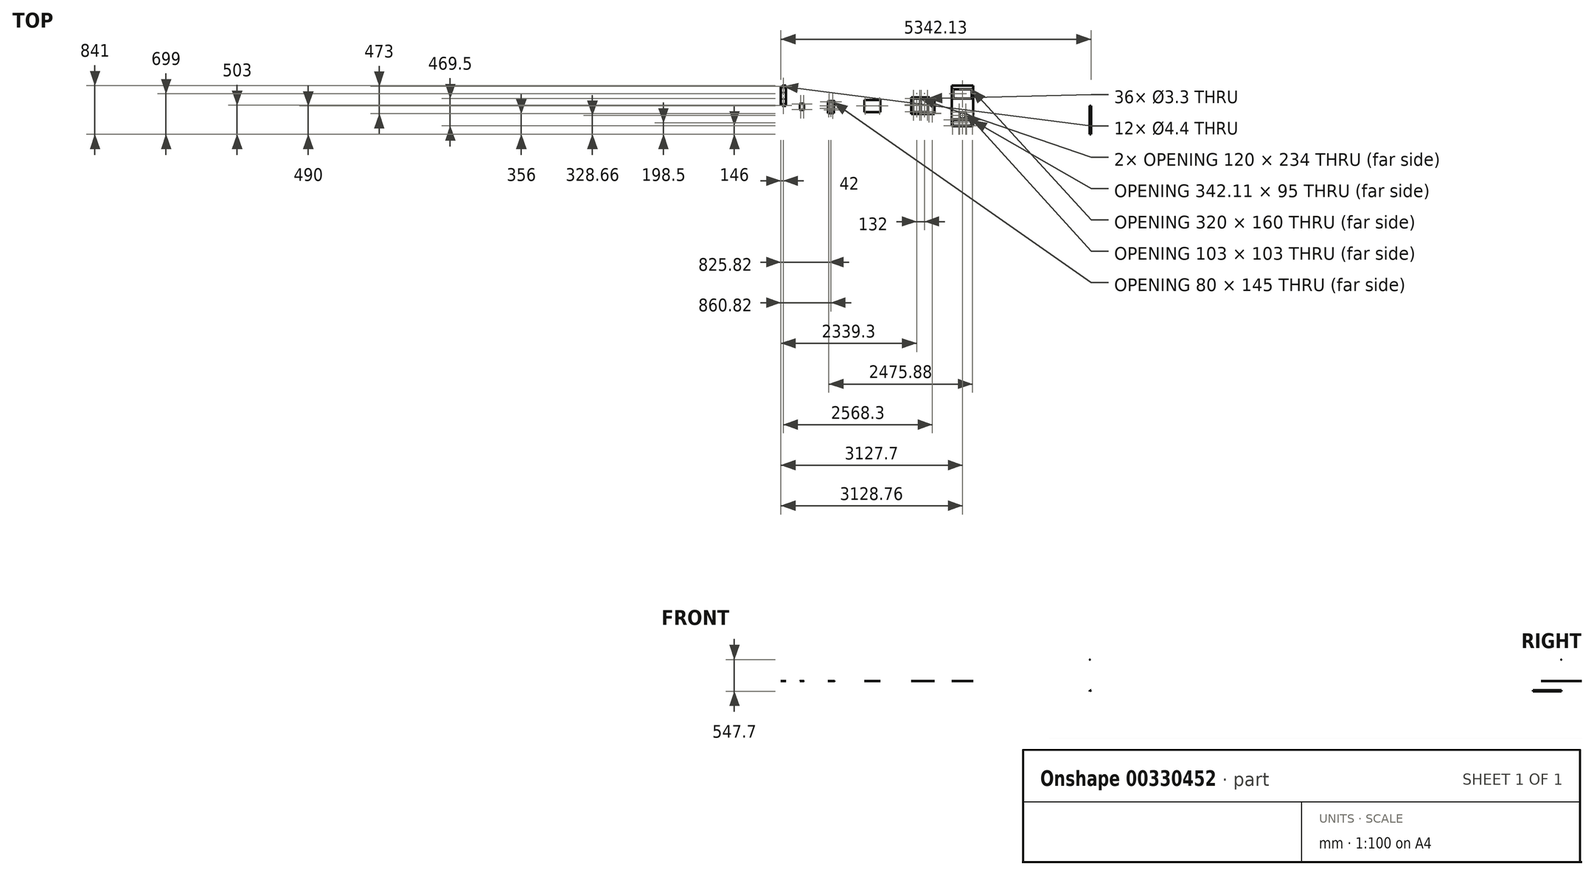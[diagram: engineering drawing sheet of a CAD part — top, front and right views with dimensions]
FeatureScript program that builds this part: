
annotation { "Feature Type Name" : "Feature", "Feature Type Description" : "" }
export const myFeature = defineFeature(function(context is Context, id is Id, definition is map)
    precondition{}
    {
        {
            var Q0;
            Q0=qCreatedBy(makeId("Top.planeOp"),FACE);
            var sketch = newSketch(context, id + "F0", { "sketchPlane" : qUnion([Q0])});
            skLineSegment(sketch, "E0.bottom", {"start": v(-184, -349) * mm, "end": v(-170, -349) * mm});
            skLineSegment(sketch, "E0.top", {"start": v(-184, 349) * mm, "end": v(184, 349) * mm});
            skLineSegment(sketch, "E0.left", {"start": v(-184, -349) * mm, "end": v(-184, 349) * mm});
            skLineSegment(sketch, "E0.right", {"start": v(184, -349) * mm, "end": v(184, 349) * mm});
            skPoint(sketch, "E0.middle", {"position": v(0, 0) * mm});
            skPoint(sketch, "E1.endSnap0", {"position": v(0, 349) * mm});
            skPoint(sketch, "E2.endSnap0", {"position": v(-184, 0) * mm});
            skPoint(sketch, "E3.positionSnap0", {"position": v(184, 0) * mm});
            skPoint(sketch, "E4", {"position": v(-170, -349) * mm});
            skPoint(sketch, "E5", {"position": v(-170, -244) * mm});
            skLineSegment(sketch, "E6", {"start": v(-165, -244) * mm, "end": v(0, -244) * mm});
            skLineSegment(sketch, "E7.MirrorCS", {"start": v(165.12, -244) * mm, "end": v(0, -244) * mm});
            skPoint(sketch, "E1.start.orphan", {"position": v(0, 349) * mm});
            skLineSegment(sketch, "E8.trimOffspring", {"start": v(170, -349) * mm, "end": v(184, -349) * mm});
            skLineSegment(sketch, "E9", {"start": v(170, -349) * mm, "end": v(-170, -349) * mm});
            skLineSegment(sketch, "E10", {"start": v(167.11, -339) * mm, "end": v(-164.96, -339) * mm});
            skLineSegment(sketch, "E11", {"start": v(170.11, -248.88) * mm, "end": v(172.11, -333.88) * mm});
            skLineSegment(sketch, "E12", {"start": v(-170, -249) * mm, "end": v(-169.96, -334) * mm});
            skPoint(sketch, "E13.visualSharp", {"position": v(172.23, -339) * mm});
            skArc(sketch, "E13.filletArc", {"start": v(167.11, -339) * mm, "mid": v(170.69, -337.5) * mm, "end": v(172.11, -333.88) * mm});
            skPoint(sketch, "E14.visualSharp", {"position": v(170, -244) * mm});
            skArc(sketch, "E14.filletArc", {"start": v(170.11, -248.88) * mm, "mid": v(168.6, -245.42) * mm, "end": v(165.12, -244) * mm});
            skArc(sketch, "E15.filletArc", {"start": v(-165, -244) * mm, "mid": v(-168.53, -245.47) * mm, "end": v(-170, -249) * mm});
            skPoint(sketch, "E16.visualSharp", {"position": v(-169.96, -339) * mm});
            skArc(sketch, "E16.filletArc", {"start": v(-169.96, -334) * mm, "mid": v(-168.5, -337.54) * mm, "end": v(-164.96, -339) * mm});
            skLineSegment(sketch, "E17.bottom", {"start": v(155, 289) * mm, "end": v(-155, 289) * mm});
            skLineSegment(sketch, "E17.top", {"start": v(155, 129) * mm, "end": v(-155, 129) * mm});
            skLineSegment(sketch, "E17.left", {"start": v(160, 284) * mm, "end": v(160, 134) * mm});
            skLineSegment(sketch, "E17.right", {"start": v(-160, 284) * mm, "end": v(-160, 134) * mm});
            skPoint(sketch, "E17.middle", {"position": v(0, 209) * mm});
            skPoint(sketch, "E18.visualSharp", {"position": v(160, 129) * mm});
            skArc(sketch, "E18.filletArc", {"start": v(155, 129) * mm, "mid": v(158.54, 130.46) * mm, "end": v(160, 134) * mm});
            skPoint(sketch, "E19.visualSharp", {"position": v(-160, 129) * mm});
            skArc(sketch, "E19.filletArc", {"start": v(-160, 134) * mm, "mid": v(-158.54, 130.46) * mm, "end": v(-155, 129) * mm});
            skPoint(sketch, "E20.visualSharp", {"position": v(-160, 289) * mm});
            skArc(sketch, "E20.filletArc", {"start": v(-155, 289) * mm, "mid": v(-158.54, 287.54) * mm, "end": v(-160, 284) * mm});
            skPoint(sketch, "E21.visualSharp", {"position": v(160, 289) * mm});
            skArc(sketch, "E21.filletArc", {"start": v(160, 284) * mm, "mid": v(158.54, 287.54) * mm, "end": v(155, 289) * mm});
            skLineSegment(sketch, "E22", {"start": v(171.11, -291.38) * mm, "end": v(-169.98, -291.5) * mm, "construction": true});
            skPoint(sketch, "E23", {"position": v(-169, -344) * mm});
            skPoint(sketch, "E24", {"position": v(-64, -344) * mm});
            skPoint(sketch, "E25", {"position": v(-50, -344) * mm});
            skPoint(sketch, "E26", {"position": v(55, -344) * mm});
            skPoint(sketch, "E27", {"position": v(69, -344) * mm});
            skPoint(sketch, "E28", {"position": v(174, -344) * mm});
            skCircle(sketch, "E29", {"center": v(-169, -344) * mm, "radius": 1.65 * mm});
            skCircle(sketch, "E30", {"center": v(-64, -344) * mm, "radius": 1.65 * mm});
            skCircle(sketch, "E31", {"center": v(-50, -344) * mm, "radius": 1.65 * mm});
            skCircle(sketch, "E32", {"center": v(55, -344) * mm, "radius": 1.65 * mm});
            skCircle(sketch, "E33", {"center": v(69, -344) * mm, "radius": 1.65 * mm});
            skCircle(sketch, "E34", {"center": v(174, -344) * mm, "radius": 1.65 * mm});
            skPoint(sketch, "E35.MirrorP", {"position": v(54.96, -238.84) * mm});
            skPoint(sketch, "E36.MirrorP", {"position": v(68.96, -238.83) * mm});
            skPoint(sketch, "E37.MirrorP", {"position": v(173.96, -238.76) * mm});
            skCircle(sketch, "E38.MirrorC", {"center": v(-50.04, -238.92) * mm, "radius": 1.65 * mm});
            skCircle(sketch, "E39.MirrorC", {"center": v(-64.04, -238.93) * mm, "radius": 1.65 * mm});
            skPoint(sketch, "E40.MirrorP", {"position": v(-169.04, -239) * mm});
            skCircle(sketch, "E41.MirrorC", {"center": v(-169.04, -239) * mm, "radius": 1.65 * mm});
            skCircle(sketch, "E42.MirrorC", {"center": v(54.96, -238.84) * mm, "radius": 1.65 * mm});
            skCircle(sketch, "E43.MirrorC", {"center": v(68.96, -238.83) * mm, "radius": 1.65 * mm});
            skCircle(sketch, "E44.MirrorC", {"center": v(173.96, -238.76) * mm, "radius": 1.65 * mm});
            skCircle(sketch, "E45", {"center": v(54.96, -213.84) * mm, "radius": 1.65 * mm});
            skLineSegment(sketch, "E46", {"start": v(0, -244) * mm, "end": v(0, -229.93) * mm, "construction": true});
            skCircle(sketch, "E47", {"center": v(54.96, -108.84) * mm, "radius": 1.65 * mm});
            skCircle(sketch, "E48.MirrorC", {"center": v(-54.96, -213.84) * mm, "radius": 1.65 * mm});
            skCircle(sketch, "E49.MirrorC", {"center": v(-54.96, -108.84) * mm, "radius": 1.65 * mm});
            skLineSegment(sketch, "E50", {"start": v(-54.96, -108.84) * mm, "end": v(54.96, -213.84) * mm, "construction": true});
            skLineSegment(sketch, "E51.bottom", {"start": v(-46.5, -212.84) * mm, "end": v(46.5, -212.84) * mm});
            skLineSegment(sketch, "E51.top", {"start": v(-46.5, -109.84) * mm, "end": v(46.5, -109.84) * mm});
            skLineSegment(sketch, "E51.left", {"start": v(-51.5, -207.84) * mm, "end": v(-51.5, -114.84) * mm});
            skLineSegment(sketch, "E51.right", {"start": v(51.5, -207.84) * mm, "end": v(51.5, -114.84) * mm});
            skPoint(sketch, "E51.middle", {"position": v(0, -161.34) * mm});
            skPoint(sketch, "E52.visualSharp", {"position": v(51.5, -212.84) * mm});
            skArc(sketch, "E52.filletArc", {"start": v(46.5, -212.84) * mm, "mid": v(50.04, -211.38) * mm, "end": v(51.5, -207.84) * mm});
            skPoint(sketch, "E53.visualSharp", {"position": v(51.5, -109.84) * mm});
            skArc(sketch, "E53.filletArc", {"start": v(51.5, -114.84) * mm, "mid": v(50.04, -111.3) * mm, "end": v(46.5, -109.84) * mm});
            skPoint(sketch, "E54.visualSharp", {"position": v(-51.5, -109.84) * mm});
            skArc(sketch, "E54.filletArc", {"start": v(-46.5, -109.84) * mm, "mid": v(-50.04, -111.3) * mm, "end": v(-51.5, -114.84) * mm});
            skPoint(sketch, "E55.visualSharp", {"position": v(-51.5, -212.84) * mm});
            skArc(sketch, "E55.filletArc", {"start": v(-51.5, -207.84) * mm, "mid": v(-50.04, -211.38) * mm, "end": v(-46.5, -212.84) * mm});
            skSolve(sketch);
        }
        {
            var Q0;
            {var subQ1=sQuery(id+"F0.wireOp",EDGE,"E0.bottom");Q0=makeQuery(id+"F0.imprint","IMPRINT",FACE,{"disambiguationData":[TD([[makeQuery(id+"F0.imprint","IMPRINT",EDGE,{"derivedFrom":subQ1}),1.0]])]});}
            extrude(context, id + "F1", {"entities" : qUnion([Q0]), "depth" : 3 * mm});
        }
        {
            var Q0;
            Q0=qCreatedBy(makeId("Top.planeOp"),FACE);
            var sketch = newSketch(context, id + "F2", { "sketchPlane" : qUnion([Q0])});
            skLineSegment(sketch, "E56.bottom", {"start": v(-881.4, -140) * mm, "end": v(-701.4, -140) * mm});
            skLineSegment(sketch, "E56.left", {"start": v(-881.4, -140) * mm, "end": v(-881.4, 150) * mm});
            skPoint(sketch, "E56.middle", {"position": v(-788.4, 15.4) * mm});
            skPoint(sketch, "E57", {"position": v(-869.4, 150) * mm});
            skLineSegment(sketch, "E58", {"start": v(-788.4, 15.4) * mm, "end": v(-788.4, 43.03) * mm, "construction": true});
            skLineSegment(sketch, "E59", {"start": v(-788.4, 15.4) * mm, "end": v(-811.31, 15.4) * mm, "construction": true});
            skPoint(sketch, "E60", {"position": v(-869.4, 10) * mm});
            skPoint(sketch, "E61", {"position": v(-869.4, 132) * mm});
            skPoint(sketch, "E62", {"position": v(-725.4, -104) * mm});
            skPoint(sketch, "E63.MirrorP", {"position": v(-848.4, -104) * mm});
            skPoint(sketch, "E64.MirrorP", {"position": v(-725.4, 130) * mm});
            skPoint(sketch, "E65.MirrorP", {"position": v(-848.4, 130) * mm});
            skLineSegment(sketch, "E66", {"start": v(-837.4, 130) * mm, "end": v(-739.4, 130) * mm});
            skLineSegment(sketch, "E67", {"start": v(-728.4, -95) * mm, "end": v(-728.4, 1) * mm});
            skLineSegment(sketch, "E68", {"start": v(-739.4, -104) * mm, "end": v(-839.4, -104) * mm});
            skLineSegment(sketch, "E69", {"start": v(-848.4, -95) * mm, "end": v(-848.4, 1) * mm});
            skPoint(sketch, "E70", {"position": v(-848.4, -95) * mm});
            skPoint(sketch, "E71", {"position": v(-839.4, -104) * mm});
            skLineSegment(sketch, "E72", {"start": v(-837.4, -104) * mm, "end": v(-837.4, -95) * mm});
            skLineSegment(sketch, "E73", {"start": v(-837.4, -95) * mm, "end": v(-846.4, -95) * mm});
            skCircle(sketch, "E74", {"center": v(-840.9, -99.5) * mm, "radius": 1.65 * mm});
            skLineSegment(sketch, "E75.MirrorCS", {"start": v(-739.4, -104) * mm, "end": v(-739.4, -95) * mm});
            skPoint(sketch, "E76.MirrorP", {"position": v(-725.4, -95) * mm});
            skLineSegment(sketch, "E77.MirrorCS", {"start": v(-739.4, -95) * mm, "end": v(-730.4, -95) * mm});
            skCircle(sketch, "E78.MirrorC", {"center": v(-735.9, -99.5) * mm, "radius": 1.65 * mm});
            skLineSegment(sketch, "E79.MirrorCS", {"start": v(-837.4, 130) * mm, "end": v(-837.4, 121) * mm});
            skLineSegment(sketch, "E80.MirrorCS", {"start": v(-839.4, 121) * mm, "end": v(-848.4, 121) * mm});
            skCircle(sketch, "E81.MirrorC", {"center": v(-840.9, 125.5) * mm, "radius": 1.65 * mm});
            skLineSegment(sketch, "E82.MirrorCS", {"start": v(-737.4, 121) * mm, "end": v(-728.4, 121) * mm});
            skLineSegment(sketch, "E83.MirrorCS", {"start": v(-739.4, 130) * mm, "end": v(-739.4, 121) * mm});
            skCircle(sketch, "E84.MirrorC", {"center": v(-735.9, 125.5) * mm, "radius": 1.65 * mm});
            skLineSegment(sketch, "E85.MirrorCS", {"start": v(-837.4, 1) * mm, "end": v(-846.4, 1) * mm});
            skLineSegment(sketch, "E86.MirrorCS", {"start": v(-837.4, 10) * mm, "end": v(-837.4, 1) * mm});
            skCircle(sketch, "E87.MirrorC", {"center": v(-840.9, 5.5) * mm, "radius": 1.65 * mm});
            skCircle(sketch, "E88", {"center": v(-840.9, 20.5) * mm, "radius": 1.65 * mm});
            skPoint(sketch, "E89", {"position": v(-848.4, 25) * mm});
            skLineSegment(sketch, "E90", {"start": v(-846.4, 25) * mm, "end": v(-837.4, 25) * mm});
            skLineSegment(sketch, "E91", {"start": v(-837.4, 25) * mm, "end": v(-837.4, 10) * mm});
            skLineSegment(sketch, "E92.MirrorCS", {"start": v(-739.4, 1) * mm, "end": v(-730.4, 1) * mm});
            skLineSegment(sketch, "E93.MirrorCS", {"start": v(-739.4, 10) * mm, "end": v(-739.4, 1) * mm});
            skLineSegment(sketch, "E94.MirrorCS", {"start": v(-739.4, 25) * mm, "end": v(-739.4, 10) * mm});
            skLineSegment(sketch, "E95.MirrorCS", {"start": v(-730.4, 25) * mm, "end": v(-739.4, 25) * mm});
            skCircle(sketch, "E96.MirrorC", {"center": v(-735.9, 20.5) * mm, "radius": 1.65 * mm});
            skCircle(sketch, "E97.MirrorC", {"center": v(-735.9, 5.5) * mm, "radius": 1.65 * mm});
            skLineSegment(sketch, "E98", {"start": v(-848.4, 25) * mm, "end": v(-848.4, 121) * mm});
            skLineSegment(sketch, "E99", {"start": v(-728.4, 25) * mm, "end": v(-728.4, 121) * mm});
            skLineSegment(sketch, "E100", {"start": v(-737.4, 121) * mm, "end": v(-739.4, 121) * mm});
            skLineSegment(sketch, "E101", {"start": v(-837.4, 121) * mm, "end": v(-839.4, 121) * mm});
            skLineSegment(sketch, "E102", {"start": v(-728.4, 25) * mm, "end": v(-730.4, 25) * mm});
            skLineSegment(sketch, "E103", {"start": v(-730.4, 1) * mm, "end": v(-728.4, 1) * mm});
            skLineSegment(sketch, "E104", {"start": v(-846.4, 1) * mm, "end": v(-848.4, 1) * mm});
            skLineSegment(sketch, "E105", {"start": v(-846.4, 25) * mm, "end": v(-848.4, 25) * mm});
            skLineSegment(sketch, "E106", {"start": v(-730.4, -95) * mm, "end": v(-728.4, -95) * mm});
            skLineSegment(sketch, "E107", {"start": v(-846.4, -95) * mm, "end": v(-848.4, -95) * mm});
            skLineSegment(sketch, "E108.bottom", {"start": v(-759.4, -140) * mm, "end": v(-579.4, -140) * mm});
            skPoint(sketch, "E108.middle", {"position": v(-656.4, 6) * mm});
            skPoint(sketch, "E109", {"position": v(-743.4, 134) * mm});
            skLineSegment(sketch, "E110", {"start": v(-656.4, 6) * mm, "end": v(-656.4, 33.63) * mm, "construction": true});
            skLineSegment(sketch, "E111", {"start": v(-656.4, 6) * mm, "end": v(-679.31, 6) * mm, "construction": true});
            skPoint(sketch, "E112.MirrorP", {"position": v(-493.4, 30) * mm});
            skPoint(sketch, "E113.MirrorP", {"position": v(-493.4, -112) * mm});
            skPoint(sketch, "E114", {"position": v(-596.4, -104) * mm});
            skPoint(sketch, "E115.MirrorP", {"position": v(-717.4, -104) * mm});
            skPoint(sketch, "E116.MirrorP", {"position": v(-596.4, 130) * mm});
            skPoint(sketch, "E117.MirrorP", {"position": v(-717.4, 130) * mm});
            skLineSegment(sketch, "E118", {"start": v(-705.4, 130) * mm, "end": v(-607.4, 130) * mm});
            skLineSegment(sketch, "E119", {"start": v(-596.4, -95) * mm, "end": v(-596.4, 1) * mm});
            skLineSegment(sketch, "E120", {"start": v(-607.4, -104) * mm, "end": v(-705.4, -104) * mm});
            skLineSegment(sketch, "E121", {"start": v(-716.4, -95) * mm, "end": v(-716.4, 1) * mm});
            skPoint(sketch, "E122", {"position": v(-717.4, -95) * mm});
            skPoint(sketch, "E123", {"position": v(-707.4, -104) * mm});
            skLineSegment(sketch, "E124", {"start": v(-705.4, -104) * mm, "end": v(-705.4, -95) * mm});
            skLineSegment(sketch, "E125", {"start": v(-705.4, -95) * mm, "end": v(-714.4, -95) * mm});
            skCircle(sketch, "E126", {"center": v(-708.9, -99.5) * mm, "radius": 1.65 * mm});
            skLineSegment(sketch, "E127.MirrorCS", {"start": v(-607.4, -104) * mm, "end": v(-607.4, -95) * mm});
            skPoint(sketch, "E128.MirrorP", {"position": v(-596.4, -95) * mm});
            skLineSegment(sketch, "E129.MirrorCS", {"start": v(-607.4, -95) * mm, "end": v(-598.4, -95) * mm});
            skCircle(sketch, "E130.MirrorC", {"center": v(-603.9, -99.5) * mm, "radius": 1.65 * mm});
            skLineSegment(sketch, "E131.MirrorCS", {"start": v(-705.4, 130) * mm, "end": v(-705.4, 121) * mm});
            skLineSegment(sketch, "E132.MirrorCS", {"start": v(-707.4, 121) * mm, "end": v(-716.4, 121) * mm});
            skCircle(sketch, "E133.MirrorC", {"center": v(-708.9, 125.5) * mm, "radius": 1.65 * mm});
            skLineSegment(sketch, "E134.MirrorCS", {"start": v(-605.4, 121) * mm, "end": v(-596.4, 121) * mm});
            skLineSegment(sketch, "E135.MirrorCS", {"start": v(-607.4, 130) * mm, "end": v(-607.4, 121) * mm});
            skCircle(sketch, "E136.MirrorC", {"center": v(-603.9, 125.5) * mm, "radius": 1.65 * mm});
            skLineSegment(sketch, "E137.MirrorCS", {"start": v(-705.4, 1) * mm, "end": v(-714.4, 1) * mm});
            skLineSegment(sketch, "E138.MirrorCS", {"start": v(-705.4, 10) * mm, "end": v(-705.4, 1) * mm});
            skCircle(sketch, "E139.MirrorC", {"center": v(-708.9, 5.5) * mm, "radius": 1.65 * mm});
            skCircle(sketch, "E140", {"center": v(-708.9, 20.5) * mm, "radius": 1.65 * mm});
            skPoint(sketch, "E141", {"position": v(-717.4, 25) * mm});
            skLineSegment(sketch, "E142", {"start": v(-714.4, 25) * mm, "end": v(-705.4, 25) * mm});
            skLineSegment(sketch, "E143", {"start": v(-705.4, 25) * mm, "end": v(-705.4, 10) * mm});
            skLineSegment(sketch, "E144.MirrorCS", {"start": v(-607.4, 1) * mm, "end": v(-598.4, 1) * mm});
            skLineSegment(sketch, "E145.MirrorCS", {"start": v(-607.4, 10) * mm, "end": v(-607.4, 1) * mm});
            skLineSegment(sketch, "E146.MirrorCS", {"start": v(-607.4, 25) * mm, "end": v(-607.4, 10) * mm});
            skLineSegment(sketch, "E147.MirrorCS", {"start": v(-598.4, 25) * mm, "end": v(-607.4, 25) * mm});
            skCircle(sketch, "E148.MirrorC", {"center": v(-603.9, 20.5) * mm, "radius": 1.65 * mm});
            skCircle(sketch, "E149.MirrorC", {"center": v(-603.9, 5.5) * mm, "radius": 1.65 * mm});
            skLineSegment(sketch, "E150", {"start": v(-716.4, 25) * mm, "end": v(-716.4, 121) * mm});
            skLineSegment(sketch, "E151", {"start": v(-596.4, 25) * mm, "end": v(-596.4, 121) * mm});
            skLineSegment(sketch, "E152", {"start": v(-605.4, 121) * mm, "end": v(-607.4, 121) * mm});
            skLineSegment(sketch, "E153", {"start": v(-705.4, 121) * mm, "end": v(-707.4, 121) * mm});
            skLineSegment(sketch, "E154", {"start": v(-596.4, 25) * mm, "end": v(-598.4, 25) * mm});
            skLineSegment(sketch, "E155", {"start": v(-598.4, 1) * mm, "end": v(-596.4, 1) * mm});
            skLineSegment(sketch, "E156", {"start": v(-714.4, 1) * mm, "end": v(-716.4, 1) * mm});
            skLineSegment(sketch, "E157", {"start": v(-714.4, 25) * mm, "end": v(-716.4, 25) * mm});
            skLineSegment(sketch, "E158", {"start": v(-598.4, -95) * mm, "end": v(-596.4, -95) * mm});
            skLineSegment(sketch, "E159", {"start": v(-714.4, -95) * mm, "end": v(-716.4, -95) * mm});
            skLineSegment(sketch, "E160", {"start": v(-579.4, -140) * mm, "end": v(-481.4, -140) * mm});
            skLineSegment(sketch, "E161", {"start": v(-561.4, 120) * mm, "end": v(-561.4, 150) * mm});
            skCircle(sketch, "E162", {"center": v(-869.4, 132) * mm, "radius": 2.6 * mm});
            skCircle(sketch, "E163", {"center": v(-869.4, 10) * mm, "radius": 2.6 * mm});
            skCircle(sketch, "E164", {"center": v(-869.4, -111.5) * mm, "radius": 2.6 * mm});
            skCircle(sketch, "E165", {"center": v(-493.4, -112) * mm, "radius": 2.6 * mm});
            skCircle(sketch, "E166", {"center": v(-493.4, 30) * mm, "radius": 2.6 * mm});
            skCircle(sketch, "E167", {"center": v(-493.4, 100) * mm, "radius": 2.6 * mm});
            skLineSegment(sketch, "E168", {"start": v(-881.4, 150) * mm, "end": v(-561.4, 150) * mm});
            skLineSegment(sketch, "E169", {"start": v(-481.4, 120) * mm, "end": v(-481.4, -140) * mm});
            skLineSegment(sketch, "E170", {"start": v(-561.4, 120) * mm, "end": v(-481.4, 120) * mm});
            skPoint(sketch, "E171", {"position": v(-507.4, -140) * mm});
            skPoint(sketch, "E172", {"position": v(-587.4, -140) * mm});
            skLineSegment(sketch, "E173", {"start": v(-507.4, -140) * mm, "end": v(-507.4, -115.97) * mm, "construction": true});
            skLineSegment(sketch, "E174", {"start": v(-507.4, -115.97) * mm, "end": v(-587.4, -115.97) * mm, "construction": true});
            skLineSegment(sketch, "E175", {"start": v(-587.4, -115.97) * mm, "end": v(-587.4, -140) * mm, "construction": true});
            skPoint(sketch, "E176", {"position": v(-517.4, -134) * mm});
            skPoint(sketch, "E177", {"position": v(-577.4, -134) * mm});
            skPoint(sketch, "E178", {"position": v(-517.4, -124) * mm});
            skPoint(sketch, "E179", {"position": v(-577.4, -124) * mm});
            skCircle(sketch, "E180", {"center": v(-517.4, -134) * mm, "radius": 2.2 * mm});
            skCircle(sketch, "E181", {"center": v(-577.4, -134) * mm, "radius": 2.2 * mm});
            skCircle(sketch, "E182", {"center": v(-577.4, -124) * mm, "radius": 2.2 * mm});
            skCircle(sketch, "E183", {"center": v(-517.4, -124) * mm, "radius": 2.2 * mm});
            skSolve(sketch);
        }
        {
            var Q0;
            Q0=makeQuery(id+"F2.imprint","IMPRINT",FACE,{"disambiguationData":[TD([[makeQuery(id+"F2.imprint","IMPRINT",EDGE,{"derivedFrom":sQuery(id+"F2.wireOp",EDGE,"E56.bottom")}),1.0]])]});
            var Q1;
            {var subQ0=sQuery(id+"F2.wireOp",EDGE,"E85.MirrorCS");Q1=makeQuery(id+"F2.imprint","IMPRINT",FACE,{"disambiguationData":[TD([[makeQuery(id+"F2.imprint","IMPRINT",EDGE,{"derivedFrom":subQ0}),-1.0]])]});}
            var Q2;
            Q2=makeQuery(id+"F2.imprint","IMPRINT",FACE,{"disambiguationData":[TD([[makeQuery(id+"F2.imprint","IMPRINT",EDGE,{"derivedFrom":sQuery(id+"F2.wireOp",EDGE,"E72")}),1.0]])]});
            var Q3;
            {var subQ1=sQuery(id+"F2.wireOp",EDGE,"E75.MirrorCS");Q3=makeQuery(id+"F2.imprint","IMPRINT",FACE,{"disambiguationData":[TD([[makeQuery(id+"F2.imprint","IMPRINT",EDGE,{"derivedFrom":subQ1}),-1.0]])]});}
            var Q4;
            {var subQ0=sQuery(id+"F2.wireOp",EDGE,"E92.MirrorCS");Q4=makeQuery(id+"F2.imprint","IMPRINT",FACE,{"disambiguationData":[TD([[makeQuery(id+"F2.imprint","IMPRINT",EDGE,{"derivedFrom":subQ0}),1.0]])]});}
            var Q5;
            Q5=makeQuery(id+"F2.imprint","IMPRINT",FACE,{"disambiguationData":[TD([[makeQuery(id+"F2.imprint","IMPRINT",EDGE,{"derivedFrom":sQuery(id+"F2.wireOp",EDGE,"E82.MirrorCS")}),1.0]])]});
            var Q6;
            {var subQ0=sQuery(id+"F2.wireOp",EDGE,"E79.MirrorCS");Q6=makeQuery(id+"F2.imprint","IMPRINT",FACE,{"disambiguationData":[TD([[makeQuery(id+"F2.imprint","IMPRINT",EDGE,{"derivedFrom":subQ0}),-1.0]])]});}
            var Q7;
            {var subQ8=sQuery(id+"F2.wireOp",EDGE,"b7a07542-c151-47a1-9aac-a0db650fa98c.trimOffspring");Q7=makeQuery(id+"F2.imprint","IMPRINT",FACE,{"disambiguationData":[TD([[makeQuery(id+"F2.imprint","IMPRINT",EDGE,{"derivedFrom":subQ8}),-1.0]])]});}
            var Q8;
            Q8=makeQuery(id+"F2.imprint","IMPRINT",FACE,{"disambiguationData":[TD([[makeQuery(id+"F2.imprint","IMPRINT",EDGE,{"derivedFrom":sQuery(id+"F2.wireOp",EDGE,"E137.MirrorCS")}),-1.0]])]});
            var Q9;
            {var subQ2=sQuery(id+"F2.wireOp",EDGE,"E131.MirrorCS");Q9=makeQuery(id+"F2.imprint","IMPRINT",FACE,{"disambiguationData":[TD([[makeQuery(id+"F2.imprint","IMPRINT",EDGE,{"derivedFrom":subQ2}),-1.0]])]});}
            var Q10;
            {var subQ0=sQuery(id+"F2.wireOp",EDGE,"E124");Q10=makeQuery(id+"F2.imprint","IMPRINT",FACE,{"disambiguationData":[TD([[makeQuery(id+"F2.imprint","IMPRINT",EDGE,{"derivedFrom":subQ0}),1.0]])]});}
            var Q11;
            {var subQ0=sQuery(id+"F2.wireOp",EDGE,"6039c7ff-60d5-425a-825f-1d9fe1f83fe6");Q11=makeQuery(id+"F2.imprint","IMPRINT",FACE,{"disambiguationData":[TD([[makeQuery(id+"F2.imprint","IMPRINT",EDGE,{"derivedFrom":subQ0}),-1.0]])]});}
            var Q12;
            {var subQ11=sQuery(id+"F2.wireOp",EDGE,"E108.right");Q12=makeQuery(id+"F2.imprint","IMPRINT",FACE,{"disambiguationData":[TD([[makeQuery(id+"F2.imprint","IMPRINT",EDGE,{"derivedFrom":subQ11}),1.0]])]});}
            var Q13;
            Q13=makeQuery(id+"F2.imprint","IMPRINT",FACE,{"disambiguationData":[TD([[makeQuery(id+"F2.imprint","IMPRINT",EDGE,{"derivedFrom":sQuery(id+"F2.wireOp",EDGE,"E134.MirrorCS")}),1.0]])]});
            var Q14;
            Q14=makeQuery(id+"F2.imprint","IMPRINT",FACE,{"disambiguationData":[TD([[makeQuery(id+"F2.imprint","IMPRINT",EDGE,{"derivedFrom":sQuery(id+"F2.wireOp",EDGE,"E144.MirrorCS")}),1.0]])]});
            var Q15;
            {var subQ3=sQuery(id+"F2.wireOp",EDGE,"E127.MirrorCS");Q15=makeQuery(id+"F2.imprint","IMPRINT",FACE,{"disambiguationData":[TD([[makeQuery(id+"F2.imprint","IMPRINT",EDGE,{"derivedFrom":subQ3}),-1.0]])]});}
            var Q16;
            Q16=makeQuery(id+"F2.imprint","IMPRINT",FACE,{"disambiguationData":[TD([[makeQuery(id+"F2.imprint","IMPRINT",EDGE,{"derivedFrom":sQuery(id+"F2.wireOp",EDGE,"E108.right")}),-1.0]])]});
            extrude(context, id + "F3", {"entities" : qUnion([Q0, Q1, Q2, Q3, Q4, Q5, Q6, Q7, Q8, Q9, Q10, Q11, Q12, Q13, Q14, Q15, Q16]), "depth" : 3 * mm, "offsetDistance" : 25 * mm});
        }
        {
            var Q0;
            Q0=makeQuery(id+"F3.opExtrude","SWEPT_EDGE",EDGE,{"disambiguationData":[OSD([sQuery(id+"F2.wireOp",EDGE,"E79.MirrorCS"),sQuery(id+"F2.wireOp",EDGE,"E80.MirrorCS")])]});
            var Q1;
            Q1=makeQuery(id+"F3.opExtrude","SWEPT_EDGE",EDGE,{"disambiguationData":[OSD([sQuery(id+"F2.wireOp",EDGE,"E82.MirrorCS"),sQuery(id+"F2.wireOp",EDGE,"E83.MirrorCS")])]});
            var Q2;
            Q2=makeQuery(id+"F3.opExtrude","SWEPT_EDGE",EDGE,{"disambiguationData":[OSD([sQuery(id+"F2.wireOp",EDGE,"E85.MirrorCS"),sQuery(id+"F2.wireOp",EDGE,"E86.MirrorCS")])]});
            var Q3;
            Q3=makeQuery(id+"F3.opExtrude","SWEPT_EDGE",EDGE,{"disambiguationData":[OSD([sQuery(id+"F2.wireOp",EDGE,"E90"),sQuery(id+"F2.wireOp",EDGE,"E91")])]});
            var Q4;
            Q4=makeQuery(id+"F3.opExtrude","SWEPT_EDGE",EDGE,{"disambiguationData":[OSD([sQuery(id+"F2.wireOp",EDGE,"E94.MirrorCS"),sQuery(id+"F2.wireOp",EDGE,"E95.MirrorCS")])]});
            var Q5;
            Q5=makeQuery(id+"F3.opExtrude","SWEPT_EDGE",EDGE,{"disambiguationData":[OSD([sQuery(id+"F2.wireOp",EDGE,"E92.MirrorCS"),sQuery(id+"F2.wireOp",EDGE,"E93.MirrorCS")])]});
            var Q6;
            Q6=makeQuery(id+"F3.opExtrude","SWEPT_EDGE",EDGE,{"disambiguationData":[OSD([sQuery(id+"F2.wireOp",EDGE,"E72"),sQuery(id+"F2.wireOp",EDGE,"E73")])]});
            var Q7;
            Q7=makeQuery(id+"F3.opExtrude","SWEPT_EDGE",EDGE,{"disambiguationData":[OSD([sQuery(id+"F2.wireOp",EDGE,"E75.MirrorCS"),sQuery(id+"F2.wireOp",EDGE,"E77.MirrorCS")])]});
            fillet(context, id + "F4", {"entities" : qUnion([Q0, Q1, Q2, Q3, Q4, Q5, Q6, Q7]), "radius" : 4 * mm, "tangentPropagation" : true, "allowEdgeOverflow" : false});
        }
        {
            var Q0;
            Q0=sQuery(id+"F2.wireOp",VERTEX,"E60");
            var Q1;
            Q1=sQuery(id+"F2.wireOp",VERTEX,"E61");
            var Q2;
            Q2=sQuery(id+"F2.wireOp",VERTEX,"67be5dd7-ee22-4b9b-9429-68082afcb8590.MirrorP");
            var Q3;
            Q3=sQuery(id+"F2.wireOp",VERTEX,"8b13f55b-3eaa-4861-bf3b-3456bda939c50.MirrorP");
            var Q4;
            Q4=sQuery(id+"F2.wireOp",VERTEX,"436e4749-fa0c-417f-8c4c-6e13cf99566e0.MirrorP");
            var Q5;
            Q5=sQuery(id+"F2.wireOp",VERTEX,"c0d2a8f5-0cd2-4157-b591-7a4ee4df7b3c");
            var Q6;
            Q6=sQuery(id+"F2.wireOp",VERTEX,"9cf5f22b-ce8b-4c7c-8d02-be894a4be338.MirrorP");
            var Q7;
            Q7=sQuery(id+"F2.wireOp",VERTEX,"E112.MirrorP");
            var Q8;
            Q8=sQuery(id+"F2.wireOp",VERTEX,"E113.MirrorP");
            var Q9;
            Q9=makeQuery(id+"F3.opExtrude","SWEPT_BODY",BODY,{"disambiguationData":[OSD([sQuery(id+"F2.wireOp",EDGE,"E56.bottom"),sQuery(id+"F2.wireOp",EDGE,"E56.top"),sQuery(id+"F2.wireOp",EDGE,"E56.left"),sQuery(id+"F2.wireOp",EDGE,"E56.right"),sQuery(id+"F2.wireOp",EDGE,"E66"),sQuery(id+"F2.wireOp",EDGE,"E67"),sQuery(id+"F2.wireOp",EDGE,"E68"),sQuery(id+"F2.wireOp",EDGE,"E69"),sQuery(id+"F2.wireOp",EDGE,"E72"),sQuery(id+"F2.wireOp",EDGE,"E73"),sQuery(id+"F2.wireOp",EDGE,"E74"),sQuery(id+"F2.wireOp",EDGE,"E75.MirrorCS"),sQuery(id+"F2.wireOp",EDGE,"E77.MirrorCS"),sQuery(id+"F2.wireOp",EDGE,"E78.MirrorC"),sQuery(id+"F2.wireOp",EDGE,"E79.MirrorCS"),sQuery(id+"F2.wireOp",EDGE,"E80.MirrorCS"),sQuery(id+"F2.wireOp",EDGE,"E81.MirrorC"),sQuery(id+"F2.wireOp",EDGE,"E82.MirrorCS"),sQuery(id+"F2.wireOp",EDGE,"E83.MirrorCS"),sQuery(id+"F2.wireOp",EDGE,"E84.MirrorC"),sQuery(id+"F2.wireOp",EDGE,"E85.MirrorCS"),sQuery(id+"F2.wireOp",EDGE,"E86.MirrorCS"),sQuery(id+"F2.wireOp",EDGE,"E87.MirrorC"),sQuery(id+"F2.wireOp",EDGE,"E88"),sQuery(id+"F2.wireOp",EDGE,"E90"),sQuery(id+"F2.wireOp",EDGE,"E91"),sQuery(id+"F2.wireOp",EDGE,"E92.MirrorCS"),sQuery(id+"F2.wireOp",EDGE,"E93.MirrorCS"),sQuery(id+"F2.wireOp",EDGE,"E94.MirrorCS"),sQuery(id+"F2.wireOp",EDGE,"E95.MirrorCS"),sQuery(id+"F2.wireOp",EDGE,"E96.MirrorC"),sQuery(id+"F2.wireOp",EDGE,"E97.MirrorC"),sQuery(id+"F2.wireOp",EDGE,"E98"),sQuery(id+"F2.wireOp",EDGE,"E99")])]});
            hole(context, id + "F5", {"style" : HoleStyle.SIMPLE, "endStyle" : HoleEndStyle.THROUGH, "oppositeDirection" : true, "standardTappedOrClearance" : lookupTablePath({ "standard" : "ISO", "fit" : "Close", "size" : "M5", "type" : "Clearance" }), "standardBlindInLast" : lookupTablePath({ "fit" : "Close", "standard" : "ISO", "size" : "M5", "type" : "Clearance" }), "holeDiameter" : 5.25 * mm, "isTappedThrough" : true, "tappedDepth" : 12 * mm, "tapClearance" : 3, "locations" : qUnion([Q0, Q1, Q2, Q3, Q4, Q5, Q6, Q7, Q8]), "scope" : qUnion([Q9]), "startStyle" : HoleStartStyle.PART});
        }
        {
            var Q0;
            Q0=qCreatedBy(makeId("Top.planeOp"),FACE);
            var sketch = newSketch(context, id + "F6", { "sketchPlane" : qUnion([Q0])});
            skLineSegment(sketch, "E184.bottom", {"start": v(-1687.4, -105) * mm, "end": v(-1417.4, -105) * mm});
            skLineSegment(sketch, "E184.top", {"start": v(-1687.4, 105) * mm, "end": v(-1417.4, 105) * mm});
            skLineSegment(sketch, "E184.left", {"start": v(-1687.4, -105) * mm, "end": v(-1687.4, 105) * mm});
            skLineSegment(sketch, "E184.right", {"start": v(-1417.4, -105) * mm, "end": v(-1417.4, 105) * mm});
            skCircle(sketch, "E185", {"center": v(-1675.4, 0) * mm, "radius": 2.2 * mm});
            skPoint(sketch, "E185.centerSnap0", {"position": v(-1687.4, 0) * mm});
            skLineSegment(sketch, "E186", {"start": v(-1552.4, 105) * mm, "end": v(-1552.4, 76.03) * mm, "construction": true});
            skCircle(sketch, "E187.MirrorC", {"center": v(-1429.4, 0) * mm, "radius": 2.2 * mm});
            skSolve(sketch);
        }
        {
            var Q0;
            {var subQ3=sQuery(id+"F6.wireOp",EDGE,"E184.left");Q0=makeQuery(id+"F6.imprint","IMPRINT",FACE,{"disambiguationData":[TD([[makeQuery(id+"F6.imprint","IMPRINT",EDGE,{"derivedFrom":subQ3}),-1.0]])]});}
            extrude(context, id + "F7", {"entities" : qUnion([Q0]), "depth" : 3 * mm, "offsetDistance" : 25 * mm});
        }
        {
            var Q0;
            Q0=qCreatedBy(makeId("Top.planeOp"),FACE);
            var sketch = newSketch(context, id + "F8", { "sketchPlane" : qUnion([Q0])});
            skPoint(sketch, "E188.middle", {"position": v(-2266.88, 0) * mm});
            skPoint(sketch, "E189", {"position": v(-2321.88, 0) * mm});
            skPoint(sketch, "E189.positionSnap0", {"position": v(-2331.88, 0) * mm});
            skLineSegment(sketch, "E190", {"start": v(-2266.88, 0) * mm, "end": v(-2266.88, 17.94) * mm, "construction": true});
            skLineSegment(sketch, "E191", {"start": v(-2266.88, 0) * mm, "end": v(-2283.9, 0) * mm, "construction": true});
            skPoint(sketch, "E192.MirrorP", {"position": v(-2211.88, 0) * mm});
            skLineSegment(sketch, "E193.bottom", {"start": v(-2306.88, -72.5) * mm, "end": v(-2237.53, -72.5) * mm});
            skLineSegment(sketch, "E193.top", {"start": v(-2306.88, 72.5) * mm, "end": v(-2301.03, 72.5) * mm});
            skLineSegment(sketch, "E193.left", {"start": v(-2306.88, -72.5) * mm, "end": v(-2306.88, -49.65) * mm});
            skLineSegment(sketch, "E193.right", {"start": v(-2226.88, -63.85) * mm, "end": v(-2226.88, 63.85) * mm});
            skPoint(sketch, "E194", {"position": v(-2232.88, 0) * mm});
            skPoint(sketch, "E194.positionSnap0", {"position": v(-2226.88, 0) * mm});
            skPoint(sketch, "E195", {"position": v(-2232.88, 68.5) * mm});
            skPoint(sketch, "E196", {"position": v(-2232.88, -68.5) * mm});
            skPoint(sketch, "E197", {"position": v(-2296.38, 68.5) * mm});
            skPoint(sketch, "E198", {"position": v(-2301.88, -45) * mm});
            skCircle(sketch, "E199", {"center": v(-2301.88, -45) * mm, "radius": 1.65 * mm});
            skCircle(sketch, "E200", {"center": v(-2232.88, -68.5) * mm, "radius": 1.65 * mm});
            skCircle(sketch, "E201", {"center": v(-2232.88, 68.5) * mm, "radius": 1.65 * mm});
            skCircle(sketch, "E202", {"center": v(-2296.38, 68.5) * mm, "radius": 1.65 * mm});
            skArc(sketch, "E203.0", {"start": v(-2301.88, -49.65) * mm, "mid": v(-2297.23, -45) * mm, "end": v(-2301.88, -40.35) * mm});
            skArc(sketch, "E204.0", {"start": v(-2232.88, -63.85) * mm, "mid": v(-2236.17, -65.21) * mm, "end": v(-2237.53, -68.5) * mm});
            skArc(sketch, "E205.0", {"start": v(-2301.03, 68.5) * mm, "mid": v(-2296.38, 63.85) * mm, "end": v(-2291.73, 68.5) * mm});
            skLineSegment(sketch, "E206", {"start": v(-2301.88, -49.65) * mm, "end": v(-2306.88, -49.65) * mm});
            skLineSegment(sketch, "E207", {"start": v(-2301.88, -40.35) * mm, "end": v(-2306.88, -40.35) * mm});
            skLineSegment(sketch, "E208.trimOffspring", {"start": v(-2306.88, -40.35) * mm, "end": v(-2306.88, 72.5) * mm});
            skLineSegment(sketch, "E209", {"start": v(-2237.53, -68.5) * mm, "end": v(-2237.53, -72.5) * mm});
            skLineSegment(sketch, "E210", {"start": v(-2232.88, -63.85) * mm, "end": v(-2226.88, -63.85) * mm});
            skPoint(sketch, "E211.orphan", {"position": v(-2226.88, -72.5) * mm});
            skLineSegment(sketch, "E212", {"start": v(-2237.53, 68.5) * mm, "end": v(-2237.53, 72.5) * mm});
            skLineSegment(sketch, "E213", {"start": v(-2232.88, 63.85) * mm, "end": v(-2226.88, 63.85) * mm});
            skArc(sketch, "E214.trimOffspring", {"start": v(-2237.53, 68.5) * mm, "mid": v(-2236.17, 65.21) * mm, "end": v(-2232.88, 63.85) * mm});
            skPoint(sketch, "E215.orphan", {"position": v(-2226.88, 72.5) * mm});
            skLineSegment(sketch, "E216", {"start": v(-2301.03, 68.5) * mm, "end": v(-2301.03, 72.5) * mm});
            skLineSegment(sketch, "E217", {"start": v(-2291.73, 68.5) * mm, "end": v(-2291.73, 72.5) * mm});
            skLineSegment(sketch, "E218.trimOffspring", {"start": v(-2291.73, 72.5) * mm, "end": v(-2237.53, 72.5) * mm});
            skPoint(sketch, "E219", {"position": v(-2316.88, -100) * mm});
            skLineSegment(sketch, "E220", {"start": v(-2316.88, -100) * mm, "end": v(-2316.88, 82.5) * mm});
            skLineSegment(sketch, "E221", {"start": v(-2316.88, 82.5) * mm, "end": v(-2216.88, 82.5) * mm});
            skLineSegment(sketch, "E222", {"start": v(-2316.88, -100) * mm, "end": v(-2316.88, -122.5) * mm});
            skLineSegment(sketch, "E223", {"start": v(-2316.88, -122.5) * mm, "end": v(-2216.88, -122.5) * mm});
            skLineSegment(sketch, "E224", {"start": v(-2216.88, -122.5) * mm, "end": v(-2216.88, -100) * mm});
            skLineSegment(sketch, "E225", {"start": v(-2216.88, 82.5) * mm, "end": v(-2206.88, 82.5) * mm});
            skLineSegment(sketch, "E226", {"start": v(-2201.88, 77.5) * mm, "end": v(-2201.88, 5) * mm});
            skLineSegment(sketch, "E227", {"start": v(-2206.88, 0) * mm, "end": v(-2211.88, 0) * mm});
            skLineSegment(sketch, "E228", {"start": v(-2216.88, -100) * mm, "end": v(-2216.88, -5) * mm});
            skPoint(sketch, "E229.visualSharp", {"position": v(-2201.88, 0) * mm});
            skArc(sketch, "E229.filletArc", {"start": v(-2206.88, 0) * mm, "mid": v(-2203.35, 1.46) * mm, "end": v(-2201.88, 5) * mm});
            skPoint(sketch, "E230.visualSharp", {"position": v(-2216.88, 0) * mm});
            skArc(sketch, "E230.filletArc", {"start": v(-2211.88, 0) * mm, "mid": v(-2215.42, -1.46) * mm, "end": v(-2216.88, -5) * mm});
            skPoint(sketch, "E231.visualSharp", {"position": v(-2201.88, 82.5) * mm});
            skArc(sketch, "E231.filletArc", {"start": v(-2201.88, 77.5) * mm, "mid": v(-2203.35, 81.04) * mm, "end": v(-2206.88, 82.5) * mm});
            skSolve(sketch);
        }
        {
            var Q0;
            Q0=makeQuery(id+"F8.imprint","IMPRINT",FACE,{"disambiguationData":[TD([[makeQuery(id+"F8.imprint","IMPRINT",EDGE,{"derivedFrom":sQuery(id+"F8.wireOp",EDGE,"E193.bottom")}),-1.0]])]});
            extrude(context, id + "F9", {"entities" : qUnion([Q0]), "depth" : 3 * mm, "offsetDistance" : 25 * mm});
        }
        {
            var Q0;
            Q0=makeQuery(id+"F1.opExtrude","SWEPT_EDGE",EDGE,{"disambiguationData":[OSD([sQuery(id+"F0.wireOp",EDGE,"YwBx0gfF-qPXs-5yWb-SOYl-dgfzVbBaXrZP"),sQuery(id+"F0.wireOp",EDGE,"E6")])]});
            var Q1;
            Q1=makeQuery(id+"F1.opExtrude","SWEPT_EDGE",EDGE,{"disambiguationData":[OSD([sQuery(id+"F0.wireOp",EDGE,"E7.MirrorCS"),sQuery(id+"F0.wireOp",EDGE,"f12bc95e-915c-4022-aa4c-63904933bf2d0.MirrorCS")])]});
            fillet(context, id + "F10", {"entities" : qUnion([Q0, Q1]), "radius" : 5 * mm, "tangentPropagation" : true, "allowEdgeOverflow" : false});
        }
        {
            var Q0;
            Q0=qCreatedBy(makeId("Top.planeOp"),FACE);
            var sketch = newSketch(context, id + "F11", { "sketchPlane" : qUnion([Q0])});
            skLineSegment(sketch, "E232.bottom", {"start": v(-2791.43, -71.31) * mm, "end": v(-2735.43, -71.31) * mm});
            skLineSegment(sketch, "E232.top", {"start": v(-2791.43, 42.69) * mm, "end": v(-2735.43, 42.69) * mm});
            skLineSegment(sketch, "E232.left", {"start": v(-2796.43, -66.31) * mm, "end": v(-2796.43, 37.69) * mm});
            skLineSegment(sketch, "E232.right", {"start": v(-2730.43, -66.31) * mm, "end": v(-2730.43, 37.69) * mm});
            skPoint(sketch, "E232.middle", {"position": v(-2763.43, -14.31) * mm});
            skLineSegment(sketch, "E233.left", {"start": v(-2796.43, -45.31) * mm, "end": v(-2796.43, 16.69) * mm});
            skLineSegment(sketch, "E233.right", {"start": v(-2730.43, -45.31) * mm, "end": v(-2730.43, 16.69) * mm});
            skPoint(sketch, "E234", {"position": v(-2737.43, 35.69) * mm});
            skLineSegment(sketch, "E235", {"start": v(-2763.43, -14.31) * mm, "end": v(-2771.4, -14.31) * mm, "construction": true});
            skLineSegment(sketch, "E236", {"start": v(-2763.43, -14.31) * mm, "end": v(-2763.43, -7.06) * mm, "construction": true});
            skPoint(sketch, "E237.MirrorP", {"position": v(-2789.43, 35.69) * mm});
            skLineSegment(sketch, "E238.MirrorCS", {"start": v(-2763.43, -14.31) * mm, "end": v(-2755.46, -14.31) * mm, "construction": true});
            skPoint(sketch, "E239.MirrorP", {"position": v(-2737.43, -64.31) * mm});
            skPoint(sketch, "E240.MirrorP", {"position": v(-2789.43, -64.31) * mm});
            skPoint(sketch, "E241.visualSharp", {"position": v(-2730.43, 42.69) * mm});
            skArc(sketch, "E241.filletArc", {"start": v(-2730.43, 37.69) * mm, "mid": v(-2731.9, 41.23) * mm, "end": v(-2735.43, 42.69) * mm});
            skPoint(sketch, "E242.visualSharp", {"position": v(-2796.43, 42.69) * mm});
            skArc(sketch, "E242.filletArc", {"start": v(-2791.43, 42.69) * mm, "mid": v(-2794.96, 41.23) * mm, "end": v(-2796.43, 37.69) * mm});
            skPoint(sketch, "E243.visualSharp", {"position": v(-2796.43, -71.31) * mm});
            skArc(sketch, "E243.filletArc", {"start": v(-2796.43, -66.31) * mm, "mid": v(-2794.96, -69.85) * mm, "end": v(-2791.43, -71.31) * mm});
            skPoint(sketch, "E244.visualSharp", {"position": v(-2730.43, -71.31) * mm});
            skArc(sketch, "E244.filletArc", {"start": v(-2735.43, -71.31) * mm, "mid": v(-2731.9, -69.85) * mm, "end": v(-2730.43, -66.31) * mm});
            skCircle(sketch, "E245", {"center": v(-2737.43, -64.31) * mm, "radius": 2.2 * mm});
            skLineSegment(sketch, "E246", {"start": v(-2730.43, -14.31) * mm, "end": v(-2742.16, -14.31) * mm, "construction": true});
            skPoint(sketch, "E246.endSnap0", {"position": v(-2730.43, -14.31) * mm});
            skLineSegment(sketch, "E247", {"start": v(-2763.43, -71.31) * mm, "end": v(-2763.43, -58.87) * mm, "construction": true});
            skCircle(sketch, "E248.MirrorC", {"center": v(-2789.43, -64.31) * mm, "radius": 2.2 * mm});
            skCircle(sketch, "E249.MirrorC", {"center": v(-2737.43, 35.69) * mm, "radius": 2.2 * mm});
            skCircle(sketch, "E250.MirrorC", {"center": v(-2789.43, 35.69) * mm, "radius": 2.2 * mm});
            skSolve(sketch);
        }
        {
            var Q0;
            Q0=makeQuery(id+"F11.imprint","IMPRINT",FACE,{"disambiguationData":[TD([[makeQuery(id+"F11.imprint","IMPRINT",EDGE,{"derivedFrom":sQuery(id+"F11.wireOp",EDGE,"E233.bottom")}),1.0]])]});
            var Q1;
            {var subQ0=sQuery(id+"F11.wireOp",EDGE,"E232.top");Q1=makeQuery(id+"F11.imprint","IMPRINT",FACE,{"disambiguationData":[TD([[makeQuery(id+"F11.imprint","IMPRINT",EDGE,{"derivedFrom":subQ0}),-1.0]])]});}
            var Q2;
            {var subQ0=sQuery(id+"F11.wireOp",EDGE,"E232.bottom");Q2=makeQuery(id+"F11.imprint","IMPRINT",FACE,{"disambiguationData":[TD([[makeQuery(id+"F11.imprint","IMPRINT",EDGE,{"derivedFrom":subQ0}),1.0]])]});}
            extrude(context, id + "F12", {"entities" : qUnion([Q0, Q1, Q2]), "depth" : 3 * mm, "offsetDistance" : 25 * mm});
        }
        {
            var Q0;
            Q0=qCreatedBy(makeId("Front.planeOp"),FACE);
            var sketch = newSketch(context, id + "F13", { "sketchPlane" : qUnion([Q0])});
            skLineSegment(sketch, "E251", {"start": v(363.22, -219.13) * mm, "end": v(380.22, -202.13) * mm});
            skLineSegment(sketch, "E252", {"start": v(363.22, -219.13) * mm, "end": v(363.22, -222.13) * mm});
            skLineSegment(sketch, "E253", {"start": v(380.22, -202.13) * mm, "end": v(383.22, -202.13) * mm});
            skLineSegment(sketch, "E254", {"start": v(363.22, -222.13) * mm, "end": v(383.22, -202.13) * mm});
            skLineSegment(sketch, "E255", {"start": v(535.2, -172.69) * mm, "end": v(552.2, -155.69) * mm});
            skLineSegment(sketch, "E256", {"start": v(535.2, -172.69) * mm, "end": v(535.2, -176.93) * mm});
            skLineSegment(sketch, "E257", {"start": v(552.2, -155.69) * mm, "end": v(556.43, -155.69) * mm});
            skLineSegment(sketch, "E258", {"start": v(535.2, -176.93) * mm, "end": v(556.43, -155.69) * mm});
            skSolve(sketch);
        }
        {
            var Q0;
            Q0=makeQuery(id+"F13.imprint","IMPRINT",FACE,{"disambiguationData":[TD([[makeQuery(id+"F13.imprint","IMPRINT",EDGE,{"derivedFrom":sQuery(id+"F13.wireOp",EDGE,"E255")}),-1.0]])]});
            extrude(context, id + "F14", {"entities" : qUnion([Q0]), "depth" : 490 * mm});
        }
        {
            var Q0;
            Q0=makeQuery(id+"F14.opExtrude","SWEPT_FACE",FACE,{"disambiguationData":[OSD([sQuery(id+"F13.wireOp",EDGE,"E258")])]});
            var sketch = newSketch(context, id + "F15", { "sketchPlane" : qUnion([Q0])});
            skPoint(sketch, "E259", {"position": v(268.35, 487) * mm});
            skPoint(sketch, "E259.positionSnap0", {"position": v(268.35, 490) * mm});
            skCircle(sketch, "E260", {"center": v(268.35, 487) * mm, "radius": 1.7 * mm});
            skLineSegment(sketch, "E261", {"start": v(253.33, 245) * mm, "end": v(270.01, 245) * mm});
            skCircle(sketch, "E262.MirrorC", {"center": v(268.35, 3) * mm, "radius": 1.7 * mm});
            skSolve(sketch);
        }
        {
            var Q0;
            Q0=makeQuery(id+"F15.imprint","IMPRINT",FACE,{"disambiguationData":[TD([[makeQuery(id+"F15.imprint","IMPRINT",EDGE,{"derivedFrom":sQuery(id+"F15.wireOp",EDGE,"E262.MirrorC")}),-1.0]])]});
            var Q1;
            Q1=makeQuery(id+"F15.imprint","IMPRINT",FACE,{"disambiguationData":[TD([[makeQuery(id+"F15.imprint","IMPRINT",EDGE,{"derivedFrom":sQuery(id+"F15.wireOp",EDGE,"E260")}),1.0]])]});
            extrude(context, id + "F16", {"entities" : qUnion([Q0, Q1]), "operationType" : NewBodyOperationType.REMOVE, "oppositeDirection" : true, "depth" : 25 * mm});
        }
        {
            var Q0;
            Q0=qCreatedBy(makeId("Front.planeOp"),FACE);
            var sketch = newSketch(context, id + "F17", { "sketchPlane" : qUnion([Q0])});
            skLineSegment(sketch, "E263", {"start": v(533.41, 363.21) * mm, "end": v(541.9, 371.7) * mm});
            skLineSegment(sketch, "E264", {"start": v(533.41, 367.45) * mm, "end": v(537.65, 371.7) * mm});
            skLineSegment(sketch, "E265", {"start": v(533.41, 367.45) * mm, "end": v(533.41, 363.21) * mm});
            skLineSegment(sketch, "E266", {"start": v(537.65, 371.7) * mm, "end": v(541.9, 371.7) * mm});
            skSolve(sketch);
        }
        {
            var Q0;
            Q0=makeQuery(id+"F17.imprint","IMPRINT",FACE,{"disambiguationData":[TD([[makeQuery(id+"F17.imprint","IMPRINT",EDGE,{"derivedFrom":sQuery(id+"F17.wireOp",EDGE,"E263")}),1.0]])]});
            extrude(context, id + "F18", {"entities" : qUnion([Q0]), "depth" : 490 * mm});
        }
        {
            var Q0;
            Q0=makeQuery(id+"F18.opExtrude","SWEPT_FACE",FACE,{"disambiguationData":[OSD([sQuery(id+"F17.wireOp",EDGE,"E263")])]});
            var sketch = newSketch(context, id + "F19", { "sketchPlane" : qUnion([Q0])});
            skCircle(sketch, "E267", {"center": v(-487, 640) * mm, "radius": 1.7 * mm});
            skPoint(sketch, "E267.centerSnap0", {"position": v(-490, 640) * mm});
            skLineSegment(sketch, "E268", {"start": v(-245, 634) * mm, "end": v(-245, 638.18) * mm});
            skPoint(sketch, "E268.endSnap0", {"position": v(-245, 646) * mm});
            skCircle(sketch, "E269.MirrorC", {"center": v(-3, 640) * mm, "radius": 1.7 * mm});
            skSolve(sketch);
        }
        {
            var Q0;
            Q0=makeQuery(id+"F19.imprint","IMPRINT",FACE,{"disambiguationData":[TD([[makeQuery(id+"F19.imprint","IMPRINT",EDGE,{"derivedFrom":sQuery(id+"F19.wireOp",EDGE,"E269.MirrorC")}),-1.0]])]});
            var Q1;
            Q1=makeQuery(id+"F19.imprint","IMPRINT",FACE,{"disambiguationData":[TD([[makeQuery(id+"F19.imprint","IMPRINT",EDGE,{"derivedFrom":sQuery(id+"F19.wireOp",EDGE,"E267")}),1.0]])]});
            extrude(context, id + "F20", {"entities" : qUnion([Q0, Q1]), "operationType" : NewBodyOperationType.REMOVE, "oppositeDirection" : true, "depth" : 25 * mm});
        }
        {
            var Q0;
            Q0=qCreatedBy(makeId("Top.planeOp"),FACE);
            var sketch = newSketch(context, id + "F21", { "sketchPlane" : qUnion([Q0])});
            skLineSegment(sketch, "E270.left", {"start": v(-3043.7, 0) * mm, "end": v(-3043.7, 350) * mm});
            skPoint(sketch, "E271", {"position": v(-3085.7, 339) * mm});
            skCircle(sketch, "E272", {"center": v(-3085.7, 339) * mm, "radius": 2.2 * mm});
            skLineSegment(sketch, "E273", {"start": v(-3043.7, 175) * mm, "end": v(-3070.15, 175) * mm, "construction": true});
            skPoint(sketch, "E273.endSnap0", {"position": v(-3043.7, 175) * mm});
            skCircle(sketch, "E274.MirrorC", {"center": v(-3085.7, 11) * mm, "radius": 2.2 * mm});
            skLineSegment(sketch, "E275", {"start": v(-3105.7, 333.67) * mm, "end": v(-3105.7, 351) * mm});
            skLineSegment(sketch, "E276", {"start": v(-3105.7, 351) * mm, "end": v(-3105.7, 333.67) * mm});
            skLineSegment(sketch, "E277", {"start": v(-3043.7, 350) * mm, "end": v(-3105.7, 351) * mm});
            skPoint(sketch, "E278", {"position": v(-3105.7, 334) * mm});
            skPoint(sketch, "E279", {"position": v(-3110.7, 329) * mm});
            skArc(sketch, "E280", {"start": v(-3110.7, 329) * mm, "mid": v(-3107.1, 330.41) * mm, "end": v(-3105.7, 334) * mm});
            skLineSegment(sketch, "E281", {"start": v(-3110.7, 329) * mm, "end": v(-3127.7, 329) * mm});
            skLineSegment(sketch, "E282.MirrorCS", {"start": v(-3105.7, -1) * mm, "end": v(-3105.7, 16.33) * mm});
            skArc(sketch, "E283.MirrorCS", {"start": v(-3110.7, 21) * mm, "mid": v(-3107.1, 19.59) * mm, "end": v(-3105.7, 16) * mm});
            skLineSegment(sketch, "E284.MirrorCS", {"start": v(-3110.7, 21) * mm, "end": v(-3127.7, 21) * mm});
            skLineSegment(sketch, "E285", {"start": v(-3127.7, 329) * mm, "end": v(-3127.7, 21) * mm});
            skLineSegment(sketch, "E286", {"start": v(-3105.7, -1) * mm, "end": v(-3043.7, 0) * mm});
            skPoint(sketch, "E287", {"position": v(-3127.7, 31) * mm});
            skPoint(sketch, "E288", {"position": v(-3127.7, 319) * mm});
            skLineSegment(sketch, "E289", {"start": v(-3127.7, 31) * mm, "end": v(-3043.7, 31) * mm, "construction": true});
            skLineSegment(sketch, "E290", {"start": v(-3127.7, 319) * mm, "end": v(-3043.7, 319) * mm, "construction": true});
            skPoint(sketch, "E291", {"position": v(-3127.7, 136) * mm});
            skPoint(sketch, "E292", {"position": v(-3127.7, 214) * mm});
            skLineSegment(sketch, "E293", {"start": v(-3127.7, 214) * mm, "end": v(-3043.7, 214) * mm, "construction": true});
            skLineSegment(sketch, "E294", {"start": v(-3127.7, 136) * mm, "end": v(-3043.7, 136) * mm, "construction": true});
            skPoint(sketch, "E295", {"position": v(-3116.6, 120.03) * mm});
            skPoint(sketch, "E296", {"position": v(-3116.6, 43.43) * mm});
            skPoint(sketch, "E297", {"position": v(-3054.8, 120.03) * mm});
            skPoint(sketch, "E298", {"position": v(-3054.8, 43.43) * mm});
            skCircle(sketch, "E299", {"center": v(-3116.6, 120.03) * mm, "radius": 2.1 * mm});
            skCircle(sketch, "E300", {"center": v(-3054.8, 120.03) * mm, "radius": 2.1 * mm});
            skCircle(sketch, "E301", {"center": v(-3116.6, 43.43) * mm, "radius": 2.1 * mm});
            skCircle(sketch, "E302", {"center": v(-3054.8, 43.43) * mm, "radius": 2.1 * mm});
            skCircle(sketch, "E303.MirrorC", {"center": v(-3116.6, 306.57) * mm, "radius": 2.1 * mm});
            skCircle(sketch, "E304.MirrorC", {"center": v(-3054.8, 306.57) * mm, "radius": 2.1 * mm});
            skCircle(sketch, "E305.MirrorC", {"center": v(-3054.8, 229.97) * mm, "radius": 2.1 * mm});
            skCircle(sketch, "E306.MirrorC", {"center": v(-3116.6, 229.97) * mm, "radius": 2.1 * mm});
            skPoint(sketch, "E307.orphan", {"position": v(-3105.7, 21) * mm});
            skPoint(sketch, "E308.orphan", {"position": v(-3105.7, 329) * mm});
            skSolve(sketch);
        }
        {
            var Q0;
            Q0=makeQuery(id+"F21.imprint","IMPRINT",FACE,{"disambiguationData":[TD([[makeQuery(id+"F21.imprint","IMPRINT",EDGE,{"derivedFrom":sQuery(id+"F21.wireOp",EDGE,"E272")}),-1.0]])]});
            extrude(context, id + "F22", {"entities" : qUnion([Q0]), "depth" : 3 * mm, "offsetDistance" : 25 * mm});
        }
        {
            var Q0;
            Q0=makeQuery(id+"F14.opExtrude","SWEPT_BODY",BODY,{"disambiguationData":[OSD([sQuery(id+"F13.wireOp",EDGE,"E255"),sQuery(id+"F13.wireOp",EDGE,"E256"),sQuery(id+"F13.wireOp",EDGE,"E257"),sQuery(id+"F13.wireOp",EDGE,"E258")])]});
            var Q1;
            Q1=makeQuery(id+"F18.opExtrude","SWEPT_BODY",BODY,{"disambiguationData":[OSD([sQuery(id+"F17.wireOp",EDGE,"E263"),sQuery(id+"F17.wireOp",EDGE,"E264"),sQuery(id+"F17.wireOp",EDGE,"E265"),sQuery(id+"F17.wireOp",EDGE,"E266")])]});
            transform(context, id + "F23", {"entities" : qUnion([Q0, Q1]), "transformType" : TransformType.TRANSLATION_3D, "dx" : 1658 * mm, "dy" : 0 * mm, "dz" : 0 * mm, "makeCopy" : false});
        }
    });
